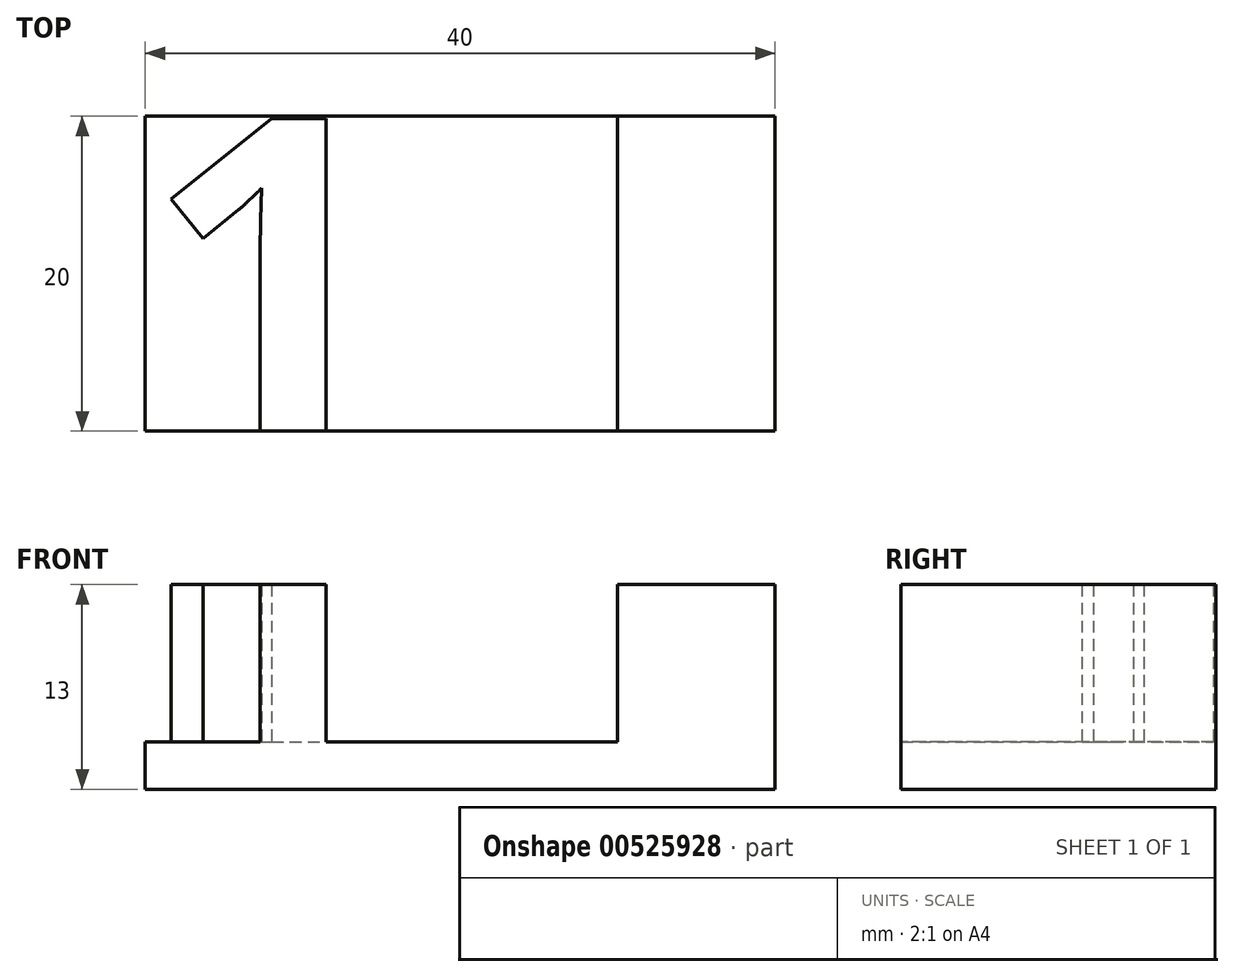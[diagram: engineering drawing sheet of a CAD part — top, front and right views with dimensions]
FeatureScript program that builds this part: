
annotation { "Feature Type Name" : "Feature", "Feature Type Description" : "" }
export const myFeature = defineFeature(function(context is Context, id is Id, definition is map)
    precondition{}
    {
        {
            var Q0;
            Q0=qCreatedBy(makeId("Top.planeOp"),FACE);
            var sketch = newSketch(context, id + "F0", { "sketchPlane" : qUnion([Q0])});
            skLineSegment(sketch, "E0.bottom", {"start": v(-11.07, 9.4) * mm, "end": v(28.93, 9.4) * mm});
            skLineSegment(sketch, "E0.top", {"start": v(-11.07, -10.6) * mm, "end": v(28.93, -10.6) * mm});
            skLineSegment(sketch, "E0.left", {"start": v(-11.07, 9.4) * mm, "end": v(-11.07, -10.6) * mm});
            skLineSegment(sketch, "E0.right", {"start": v(28.93, 9.4) * mm, "end": v(28.93, -10.6) * mm});
            skSolve(sketch);
        }
        {
            var Q0;
            Q0 = qSketchRegion(id + "F0", true);
            extrude(context, id + "F1", {"entities" : qUnion([Q0]), "depth" : 3 * mm, "offsetDistance" : 25 * mm});
        }
        {
            var Q0;
            Q0=makeQuery(id+"F1.opExtrude","CAP_FACE",FACE,{"disambiguationData":[OSD([sQuery(id+"F0.wireOp",EDGE,"E0.bottom"),sQuery(id+"F0.wireOp",EDGE,"E0.top"),sQuery(id+"F0.wireOp",EDGE,"E0.left"),sQuery(id+"F0.wireOp",EDGE,"E0.right")])],"isStart":false});
            var sketch = newSketch(context, id + "F2", { "sketchPlane" : qUnion([Q0])});
            skText(sketch, "E1", { "text": "1", "fontName": "NotoSans-Bold.ttf"});
            skLineSegment(sketch, "E2.bottom", {"start": v(28.93, 9.4) * mm, "end": v(18.93, 9.4) * mm});
            skLineSegment(sketch, "E2.top", {"start": v(28.93, -10.6) * mm, "end": v(18.93, -10.6) * mm});
            skLineSegment(sketch, "E2.left", {"start": v(28.93, 9.4) * mm, "end": v(28.93, -10.6) * mm});
            skLineSegment(sketch, "E2.right", {"start": v(18.93, 9.4) * mm, "end": v(18.93, -10.6) * mm});
            const initialGuessF2  = {"E1": [-0.01107, -0.0106, 1, 0, 0.02]};
            skSetInitialGuess(sketch, initialGuessF2);
            skSolve(sketch);
        }
        {
            var Q0;
            Q0 = qSketchRegion(id + "F2", true);
            extrude(context, id + "F3", {"entities" : qUnion([Q0]), "operationType" : NewBodyOperationType.ADD, "depth" : 10 * mm, "offsetDistance" : 25 * mm});
        }
    });
